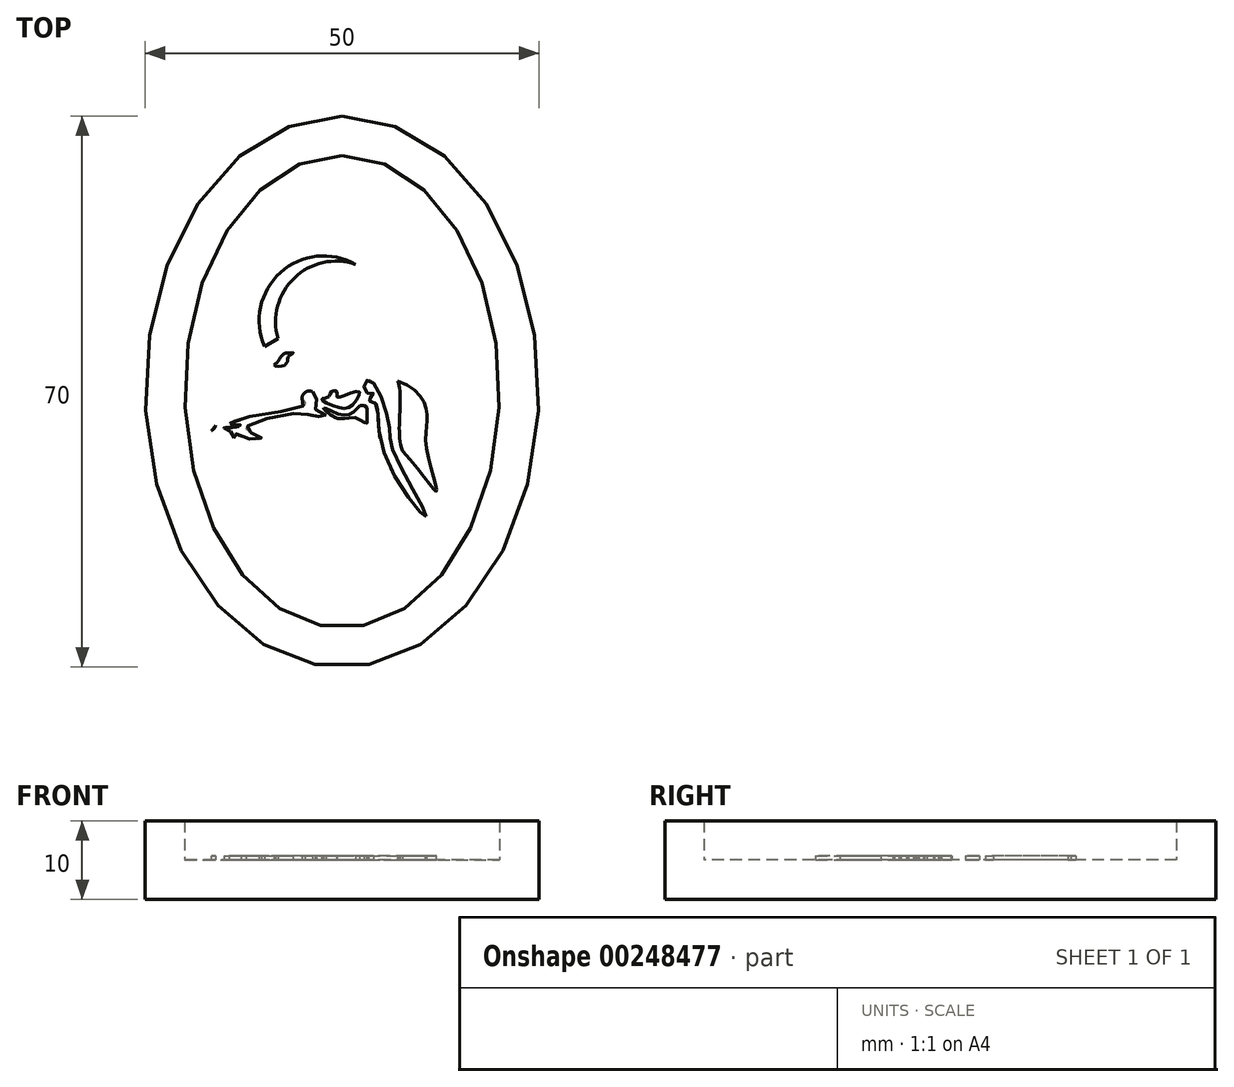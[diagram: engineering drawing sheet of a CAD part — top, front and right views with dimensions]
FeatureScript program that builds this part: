
annotation { "Feature Type Name" : "Feature", "Feature Type Description" : "" }
export const myFeature = defineFeature(function(context is Context, id is Id, definition is map)
    precondition{}
    {
        {
            var Q0;
            Q0=qCreatedBy(makeId("Top.planeOp"),FACE);
            var sketch = newSketch(context, id + "F0", { "sketchPlane" : qUnion([Q0])});
            skEllipse(sketch, "E0", {"center": v(0, 0) * mm, "majorRadius": 35 * mm, "minorRadius": 25 * mm, "majorAxis": v(0, 1)});
            skSolve(sketch);
        }
        {
            var Q0;
            Q0=makeQuery(id+"F0.imprint","IMPRINT",FACE,{"disambiguationData":[TD([[makeQuery(id+"F0.imprint","IMPRINT",EDGE,{"derivedFrom":sQuery(id+"F0.wireOp",EDGE,"E0")}),1.0]])]});
            var Q1;
            Q1 = qSketchRegion(id + "F2", true);
            extrude(context, id + "F1", {"entities" : qUnion([Q0, Q1]), "depth" : 5 * mm});
        }
        {
            var Q0;
            Q0=makeQuery(id+"F1.opExtrude","CAP_FACE",FACE,{"disambiguationData":[OSD([sQuery(id+"F0.wireOp",EDGE,"E0")])],"isStart":false});
            var sketch = newSketch(context, id + "F2", { "sketchPlane" : qUnion([Q0])});
            skEllipse(sketch, "E1", {"center": v(0, 0) * mm, "majorRadius": 30 * mm, "minorRadius": 20 * mm, "majorAxis": v(0, 1)});
            skSolve(sketch);
        }
        {
            var Q0;
            Q0=makeQuery(id+"F2.imprint","IMPRINT",FACE,{"disambiguationData":[TD([[makeQuery(id+"F2.imprint","IMPRINT",EDGE,{"derivedFrom":sQuery(id+"F2.wireOp",EDGE,"E1")}),-1.0]])]});
            extrude(context, id + "F3", {"entities" : qUnion([Q0]), "operationType" : NewBodyOperationType.ADD, "depth" : 5 * mm});
        }
        {
            var Q0;
            Q0=makeQuery(id+"F1.opExtrude","CAP_FACE",FACE,{"disambiguationData":[OSD([sQuery(id+"F0.wireOp",EDGE,"E0")])],"isStart":false});
            var sketch = newSketch(context, id + "F4", { "sketchPlane" : qUnion([Q0])});
            skArc(sketch, "E2", {"start": v(-16.12, -2.65) * mm, "mid": v(-14.25, -1.87) * mm, "end": v(-13.48, 0) * mm});
            skPoint(sketch, "E2.centerSnap0", {"position": v(-20, 0) * mm});
            skArc(sketch, "E3", {"start": v(-13.48, 0) * mm, "mid": v(-11.64, 0.52) * mm, "end": v(-11.44, 2.42) * mm});
            skArc(sketch, "E4", {"start": v(-11.44, 2.42) * mm, "mid": v(-9.69, 3.37) * mm, "end": v(-8.25, 4.76) * mm});
            skArc(sketch, "E5", {"start": v(-8.25, 4.76) * mm, "mid": v(-7, 5.93) * mm, "end": v(-6.06, 7.38) * mm});
            skLineSegment(sketch, "E6", {"start": v(-6.06, 7.38) * mm, "end": v(-5.38, 5.94) * mm});
            skArc(sketch, "E7", {"start": v(-5.38, 5.94) * mm, "mid": v(-3.9, 8.66) * mm, "end": v(-1.22, 10.2) * mm});
            skArc(sketch, "E8", {"start": v(-1.22, 10.2) * mm, "mid": v(-2.66, 8.27) * mm, "end": v(-3.64, 6.08) * mm});
            skArc(sketch, "E9", {"start": v(-3.64, 6.08) * mm, "mid": v(-2.2, 7.93) * mm, "end": v(0, 8.72) * mm});
            skPoint(sketch, "E10.2.internal.snap0", {"position": v(-2.66, 8.27) * mm});
            skFitSpline(sketch, "E10", {"points": [v(0, 8.72) * mm, v(-1.76, 6.64) * mm, v(1.94, 8.27) * mm], "startDerivative": vector(-8.09, -7) * mm, "endDerivative": vector(10.58, 8.2) * mm});
            skFitSpline(sketch, "E11", {"points": [v(1.94, 8.27) * mm, v(5.23, 9.78) * mm, v(4.05, 8.27) * mm], "startDerivative": vector(10.12, -0.4) * mm, "endDerivative": vector(-6.93, -0.16) * mm});
            skLineSegment(sketch, "E12", {"start": v(3.89, 8.2) * mm, "end": v(10.65, 8.78) * mm});
            skArc(sketch, "E13", {"start": v(1.74, 16.18) * mm, "mid": v(-7.82, 15.13) * mm, "end": v(-9.85, 5.73) * mm});
            skArc(sketch, "E14", {"start": v(1.74, 16.18) * mm, "mid": v(-6.06, 14.44) * mm, "end": v(-8.14, 6.73) * mm});
            skLineSegment(sketch, "E15", {"start": v(-9.85, 5.73) * mm, "end": v(-8.14, 6.73) * mm});
            skLineSegment(sketch, "E16", {"start": v(-3.9, 10.85) * mm, "end": v(-3.38, 10.85) * mm});
            skPoint(sketch, "E16.startSnap0", {"position": v(-3.9, 8.66) * mm});
            skLineSegment(sketch, "E17", {"start": v(10.65, 8.78) * mm, "end": v(13.6, 10.63) * mm});
            skArc(sketch, "E18", {"start": v(4.86, 5.3) * mm, "mid": v(10.28, 6.25) * mm, "end": v(13.6, 10.63) * mm});
            skArc(sketch, "E19", {"start": v(11.81, -5.03) * mm, "mid": v(10.47, 1.57) * mm, "end": v(4.86, 5.3) * mm});
            skArc(sketch, "E20", {"start": v(11.81, -5.03) * mm, "mid": v(10.6, -0.43) * mm, "end": v(6.39, 1.8) * mm});
            skArc(sketch, "E21", {"start": v(6.39, 1.8) * mm, "mid": v(6.9, -1.14) * mm, "end": v(6.68, -4.1) * mm});
            skArc(sketch, "E22", {"start": v(3.93, 2.2) * mm, "mid": v(5.84, -0.72) * mm, "end": v(6.68, -4.1) * mm});
            skArc(sketch, "E23", {"start": v(3.93, 2.2) * mm, "mid": v(2.68, 2.19) * mm, "end": v(1.6, 1.57) * mm});
            skPoint(sketch, "E23.endSnap0", {"position": v(10.47, 1.57) * mm});
            skFitSpline(sketch, "E24", {"points": [v(7.07, 1.35) * mm, v(10.79, -2.7) * mm, v(10.69, -6.92) * mm, v(12, -12.65) * mm, v(7.65, -7.53) * mm], "startDerivative": vector(30.94, -9.84) * mm, "endDerivative": vector(-23.16, 23.68) * mm});
            skFitSpline(sketch, "E25", {"points": [v(7.07, 1.35) * mm, v(7.65, -7.53) * mm], "startDerivative": vector(2.55, -6.42) * mm, "endDerivative": vector(2.83, -9.05) * mm});
            skFitSpline(sketch, "E26", {"points": [v(-16.12, -2.65) * mm, v(-16.54, -4.92) * mm], "startDerivative": vector(0.5, -3.05) * mm, "endDerivative": vector(-2.03, -1.02) * mm});
            skLineSegment(sketch, "E27", {"start": v(1.6, 1.57) * mm, "end": v(2.25, 0.92) * mm});
            skLineSegment(sketch, "E28", {"start": v(2.25, 0.92) * mm, "end": v(0, 0) * mm});
            skFitSpline(sketch, "E29", {"points": [v(0, 0) * mm, v(-1.98, 0) * mm], "startDerivative": vector(-1.98, 0) * mm, "endDerivative": vector(-2.54, -4.02) * mm});
            skFitSpline(sketch, "E30", {"points": [v(-16.54, -4.92) * mm, v(-12.05, -2.3) * mm, v(-10.2, -1.45) * mm], "startDerivative": vector(11.18, 14.9) * mm, "endDerivative": vector(4.87, -1.08) * mm});
            skLineSegment(sketch, "E31", {"start": v(-10.2, -1.45) * mm, "end": v(-5.87, -0.6) * mm});
            skFitSpline(sketch, "E32", {"points": [v(-5.87, -0.6) * mm, v(-1.98, 0) * mm], "startDerivative": vector(3.56, 6.35) * mm, "endDerivative": vector(4.32, -4.53) * mm});
            skFitSpline(sketch, "E33", {"points": [v(10.66, -15.84) * mm, v(6.46, -7.44) * mm, v(5.97, -4.1) * mm, v(3.6, 1.44) * mm, v(2.8, 0.92) * mm, v(3.34, -0.24) * mm, v(4, -0.24) * mm, v(3.34, -1.1) * mm, v(4.08, -1.34) * mm, v(5.27, -7.6) * mm, v(10.66, -15.84) * mm]});
            skFitSpline(sketch, "E34", {"points": [v(-1.63, -0.62) * mm, v(-1.4, 0) * mm, v(-0.66, 0) * mm, v(-0.66, -0.62) * mm, v(0, -0.62) * mm, v(2.18, 0) * mm, v(1.3, -1.73) * mm, v(-0.66, -1.97) * mm, v(-2.58, -0.94) * mm, v(-1.63, -0.62) * mm]});
            skFitSpline(sketch, "E35", {"points": [v(-2.34, -2.05) * mm, v(-0.66, -2.76) * mm, v(1.3, -2.68) * mm, v(2.41, -1.73) * mm, v(3.14, -1.97) * mm, v(3.14, -2.6) * mm, v(3.14, -4.03) * mm, v(1.86, -3.36) * mm, v(-0.66, -3.36) * mm, v(-2.34, -2.05) * mm]});
            skFitSpline(sketch, "E36", {"points": [v(-8.62, 3.37) * mm, v(-8.12, 3.83) * mm, v(-7.87, 4.33) * mm, v(-7.31, 4.83) * mm, v(-6.66, 4.93) * mm, v(-6.2, 4.93) * mm, v(-6.76, 4.53) * mm, v(-6.96, 3.78) * mm, v(-7.67, 3.22) * mm, v(-8.62, 3.37) * mm]});
            skArc(sketch, "E37", {"start": v(-3.74, 0) * mm, "mid": v(-4.65, -0.06) * mm, "end": v(-5.09, -0.85) * mm});
            skFitSpline(sketch, "E38", {"points": [v(-5.09, -0.85) * mm, v(-4.8, -1.7) * mm, v(-13.8, -3.72) * mm, v(-14.3, -4.28) * mm, v(-13.8, -4.13) * mm, v(-12.85, -4.28) * mm, v(-13.96, -4.53) * mm, v(-15.01, -4.63) * mm, v(-14.16, -5.08) * mm, v(-13.7, -5.84) * mm, v(-13.55, -5.28) * mm, v(-13.05, -5.69) * mm, v(-10.23, -5.89) * mm, v(-12, -4.98) * mm, v(-11.94, -4.33) * mm, v(-4.8, -2.72) * mm, v(-3.79, -3.12) * mm, v(-2.03, -3.02) * mm, v(-3.29, -2.42) * mm, v(-3.24, -0.85) * mm, v(-3.74, 0) * mm], "startDerivative": vector(21.31, -23.17) * mm, "endDerivative": vector(-18.48, 17.68) * mm});
            skSolve(sketch);
        }
        {
            var Q0;
            Q0=makeQuery(id+"F4.imprint","IMPRINT",FACE,{"disambiguationData":[TD([[makeQuery(id+"F4.imprint","IMPRINT",EDGE,{"derivedFrom":sQuery(id+"F4.wireOp",EDGE,"E13")}),-1.0]])]});
            var sketch = newSketch(context, id + "F5", { "sketchPlane" : qUnion([Q0])});
            skSolve(sketch);
        }
        {
            var Q0;
            Q0=makeQuery(id+"F4.imprint","IMPRINT",FACE,{"disambiguationData":[TD([[makeQuery(id+"F4.imprint","IMPRINT",EDGE,{"derivedFrom":sQuery(id+"F4.wireOp",EDGE,"E13")}),1.0]])]});
            var Q1;
            Q1=makeQuery(id+"F5.imprint","IMPRINT",FACE,{"disambiguationData":[TD([[makeQuery(id+"F5.imprint","IMPRINT",EDGE,{"derivedFrom":makeQuery(id+"F4.imprint","IMPRINT",EDGE,{"derivedFrom":sQuery(id+"F4.wireOp",EDGE,"E33")})}),1.0]])]});
            var Q2;
            Q2=makeQuery(id+"F5.imprint","IMPRINT",FACE,{"disambiguationData":[TD([[makeQuery(id+"F5.imprint","IMPRINT",EDGE,{"derivedFrom":makeQuery(id+"F4.imprint","IMPRINT",EDGE,{"derivedFrom":sQuery(id+"F4.wireOp",EDGE,"E13")})}),1.0]])]});
            var Q3;
            Q3=makeQuery(id+"F5.imprint","IMPRINT",FACE,{"disambiguationData":[TD([[makeQuery(id+"F5.imprint","IMPRINT",EDGE,{"derivedFrom":makeQuery(id+"F4.imprint","IMPRINT",EDGE,{"derivedFrom":sQuery(id+"F4.wireOp",EDGE,"E24")})}),-1.0]])]});
            var Q4;
            Q4=makeQuery(id+"F4.imprint","IMPRINT",FACE,{"disambiguationData":[TD([[makeQuery(id+"F4.imprint","IMPRINT",EDGE,{"derivedFrom":sQuery(id+"F4.wireOp",EDGE,"E33")}),1.0]])]});
            var Q5;
            Q5=makeQuery(id+"F5.imprint","IMPRINT",FACE,{"disambiguationData":[TD([[makeQuery(id+"F5.imprint","IMPRINT",EDGE,{"derivedFrom":makeQuery(id+"F4.imprint","IMPRINT",EDGE,{"derivedFrom":sQuery(id+"F4.wireOp",EDGE,"E37")})}),1.0]])]});
            var Q6;
            Q6=makeQuery(id+"F4.imprint","IMPRINT",FACE,{"disambiguationData":[TD([[makeQuery(id+"F4.imprint","IMPRINT",EDGE,{"derivedFrom":sQuery(id+"F4.wireOp",EDGE,"E24")}),-1.0]])]});
            var Q7;
            Q7=makeQuery(id+"F5.imprint","IMPRINT",FACE,{"disambiguationData":[TD([[makeQuery(id+"F5.imprint","IMPRINT",EDGE,{"derivedFrom":makeQuery(id+"F4.imprint","IMPRINT",EDGE,{"derivedFrom":sQuery(id+"F4.wireOp",EDGE,"E35")})}),-1.0]])]});
            var Q8;
            Q8=makeQuery(id+"F4.imprint","IMPRINT",FACE,{"disambiguationData":[TD([[makeQuery(id+"F4.imprint","IMPRINT",EDGE,{"derivedFrom":sQuery(id+"F4.wireOp",EDGE,"E37")}),1.0]])]});
            var Q9;
            Q9=makeQuery(id+"F5.imprint","IMPRINT",FACE,{"disambiguationData":[TD([[makeQuery(id+"F5.imprint","IMPRINT",EDGE,{"derivedFrom":makeQuery(id+"F4.imprint","IMPRINT",EDGE,{"derivedFrom":sQuery(id+"F4.wireOp",EDGE,"E36")})}),-1.0]])]});
            var Q10;
            {var subQ0=sQuery(id+"F4.wireOp",EDGE,"E30");var subQ1=sQuery(id+"F4.wireOp",EDGE,"E26");var subQ2=makeQuery(id+"F4.imprint","INTERSECT",VERTEX,{"disambiguationData":[OD(0.0)],"derivedFrom":[subQ1,subQ0]});Q10=makeQuery(id+"F5.imprint","IMPRINT",FACE,{"disambiguationData":[TD([[makeQuery(id+"F5.imprint","IMPRINT",EDGE,{"derivedFrom":makeQuery(id+"F4.imprint","IMPRINT",EDGE,{"disambiguationData":[TD([[subQ2,1.0]])],"derivedFrom":subQ1})}),-1.0]])]});}
            var Q11;
            Q11=makeQuery(id+"F4.imprint","IMPRINT",FACE,{"disambiguationData":[TD([[makeQuery(id+"F4.imprint","IMPRINT",EDGE,{"derivedFrom":sQuery(id+"F4.wireOp",EDGE,"E35")}),-1.0]])]});
            var Q12;
            Q12=makeQuery(id+"F5.imprint","IMPRINT",FACE,{"disambiguationData":[TD([[makeQuery(id+"F5.imprint","IMPRINT",EDGE,{"derivedFrom":makeQuery(id+"F4.imprint","IMPRINT",EDGE,{"derivedFrom":sQuery(id+"F4.wireOp",EDGE,"E34")})}),-1.0]])]});
            var Q13;
            {var subQ0=sQuery(id+"F4.wireOp",EDGE,"E30");var subQ1=sQuery(id+"F4.wireOp",EDGE,"E26");var subQ2=makeQuery(id+"F4.imprint","INTERSECT",VERTEX,{"disambiguationData":[OD(0.0)],"derivedFrom":[subQ1,subQ0]});Q13=makeQuery(id+"F4.imprint","IMPRINT",FACE,{"disambiguationData":[TD([[makeQuery(id+"F4.imprint","IMPRINT",EDGE,{"disambiguationData":[TD([[subQ2,1.0]])],"derivedFrom":subQ1}),-1.0]])]});}
            var Q14;
            Q14=makeQuery(id+"F4.imprint","IMPRINT",FACE,{"disambiguationData":[TD([[makeQuery(id+"F4.imprint","IMPRINT",EDGE,{"derivedFrom":sQuery(id+"F4.wireOp",EDGE,"E36")}),-1.0]])]});
            var Q15;
            Q15=makeQuery(id+"F4.imprint","IMPRINT",FACE,{"disambiguationData":[TD([[makeQuery(id+"F4.imprint","IMPRINT",EDGE,{"derivedFrom":sQuery(id+"F4.wireOp",EDGE,"E34")}),-1.0]])]});
            extrude(context, id + "F6", {"entities" : qUnion([Q0, Q1, Q2, Q3, Q4, Q5, Q6, Q7, Q8, Q9, Q10, Q11, Q12, Q13, Q14, Q15]), "operationType" : NewBodyOperationType.ADD, "depth" : 0.5 * mm});
        }
    });
